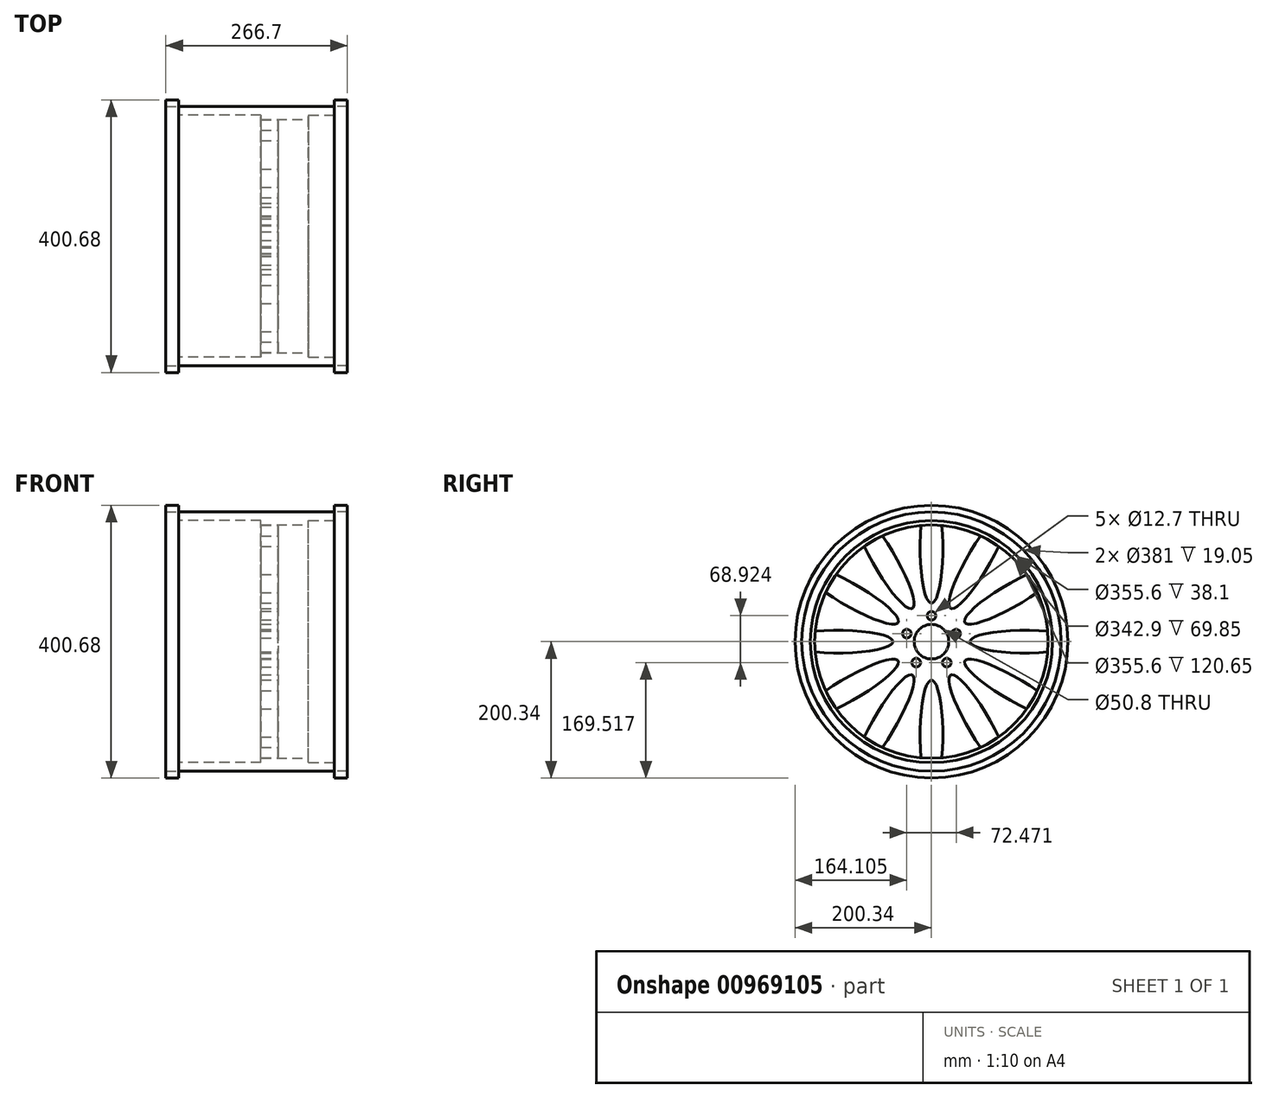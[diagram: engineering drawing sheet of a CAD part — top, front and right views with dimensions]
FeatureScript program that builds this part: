
annotation { "Feature Type Name" : "Feature", "Feature Type Description" : "" }
export const myFeature = defineFeature(function(context is Context, id is Id, definition is map)
    precondition{}
    {
        {
            var Q0;
            Q0=qCreatedBy(makeId("Right.planeOp"),FACE);
            var sketch = newSketch(context, id + "F0", { "sketchPlane" : qUnion([Q0])});
            skCircle(sketch, "E0", {"center": v(0, 0) * mm, "radius": 190.5 * mm});
            skSolve(sketch);
        }
        {
            var Q0;
            Q0=makeQuery(id+"F0.imprint","IMPRINT",FACE,{"disambiguationData":[TD([[makeQuery(id+"F0.imprint","IMPRINT",EDGE,{"derivedFrom":sQuery(id+"F0.wireOp",EDGE,"E0")}),1.0]])]});
            extrude(context, id + "F1", {"entities" : qUnion([Q0]), "depth" : 228.6 * mm, "offsetDistance" : 25.4 * mm});
        }
        {
            var Q0;
            Q0=makeQuery(id+"F1.opExtrude","CAP_FACE",FACE,{"disambiguationData":[OSD([sQuery(id+"F0.wireOp",EDGE,"E0")])],"isStart":false});
            var sketch = newSketch(context, id + "F2", { "sketchPlane" : qUnion([Q0])});
            skCircle(sketch, "E1", {"center": v(0, 0) * mm, "radius": 200.34 * mm});
            skSolve(sketch);
        }
        {
            var Q0;
            Q0=makeQuery(id+"F2.imprint","IMPRINT",FACE,{"disambiguationData":[TD([[makeQuery(id+"F2.imprint","IMPRINT",EDGE,{"derivedFrom":sQuery(id+"F2.wireOp",EDGE,"E1")}),1.0]])]});
            extrude(context, id + "F3", {"entities" : qUnion([Q0]), "depth" : 19.05 * mm, "offsetDistance" : 25.4 * mm});
        }
        {
            var Q0;
            Q0=makeQuery(id+"F1.opExtrude","CAP_FACE",FACE,{"disambiguationData":[OSD([sQuery(id+"F0.wireOp",EDGE,"E0")])],"isStart":false});
            var sketch = newSketch(context, id + "F4", { "sketchPlane" : qUnion([Q0])});
            skCircle(sketch, "E2", {"center": v(0, 0) * mm, "radius": 177.8 * mm});
            skSolve(sketch);
        }
        {
            var Q0;
            Q0 = qSketchRegion(id + "F4", true);
            extrude(context, id + "F5", {"entities" : qUnion([Q0]), "operationType" : NewBodyOperationType.REMOVE, "oppositeDirection" : true, "depth" : 38.1 * mm, "offsetDistance" : 25.4 * mm});
        }
        {
            var Q0;
            Q0=makeQuery(id+"F5.boolean.opBoolean","COPY",FACE,{"derivedFrom":makeQuery(id+"F5.opExtrude","CAP_FACE",FACE,{"disambiguationData":[OSD([sQuery(id+"F4.wireOp",EDGE,"E2")])],"isStart":false})});
            var sketch = newSketch(context, id + "F6", { "sketchPlane" : qUnion([Q0])});
            skCircle(sketch, "E3", {"center": v(0, 0) * mm, "radius": 171.45 * mm});
            skSolve(sketch);
        }
        {
            var Q0;
            Q0 = qSketchRegion(id + "F6", true);
            extrude(context, id + "F7", {"entities" : qUnion([Q0]), "operationType" : NewBodyOperationType.REMOVE, "oppositeDirection" : true, "depth" : 44.45 * mm, "offsetDistance" : 25.4 * mm});
        }
        {
            var Q0;
            Q0=makeQuery(id+"F1.opExtrude","CAP_FACE",FACE,{"disambiguationData":[OSD([sQuery(id+"F0.wireOp",EDGE,"E0")])],"isStart":true});
            var sketch = newSketch(context, id + "F8", { "sketchPlane" : qUnion([Q0])});
            skCircle(sketch, "E4", {"center": v(0, 0) * mm, "radius": 200.34 * mm});
            skCircle(sketch, "E5", {"center": v(0, 0) * mm, "radius": 190.5 * mm});
            skSolve(sketch);
        }
        {
            var Q0;
            Q0 = qSketchRegion(id + "F8", true);
            extrude(context, id + "F9", {"entities" : qUnion([Q0]), "depth" : 19.05 * mm, "offsetDistance" : 25.4 * mm});
        }
        {
            var Q0;
            Q0=makeQuery(id+"F7.boolean.opBoolean","COPY",FACE,{"derivedFrom":makeQuery(id+"F7.opExtrude","CAP_FACE",FACE,{"disambiguationData":[OSD([sQuery(id+"F6.wireOp",EDGE,"E3")])],"isStart":false})});
            var sketch = newSketch(context, id + "F10", { "sketchPlane" : qUnion([Q0])});
            skSolve(sketch);
        }
        {
            var Q0;
            Q0=qCreatedBy(makeId("Right.planeOp"),FACE);
            var sketch = newSketch(context, id + "F11", { "sketchPlane" : qUnion([Q0])});
            skCircle(sketch, "E6", {"center": v(0, 0) * mm, "radius": 177.8 * mm});
            skSolve(sketch);
        }
        {
            var Q0;
            Q0=makeQuery(id+"F11.imprint","IMPRINT",FACE,{"disambiguationData":[TD([[makeQuery(id+"F11.imprint","IMPRINT",EDGE,{"derivedFrom":sQuery(id+"F11.wireOp",EDGE,"E6")}),1.0]])]});
            extrude(context, id + "F12", {"entities" : qUnion([Q0]), "operationType" : NewBodyOperationType.REMOVE, "depth" : 120.65 * mm, "offsetDistance" : 25.4 * mm});
        }
        {
            var Q0;
            Q0=makeQuery(id+"F10.imprint","IMPRINT",FACE,{"disambiguationData":[TD([[makeQuery(id+"F10.imprint","IMPRINT",EDGE,{"derivedFrom":makeQuery(id+"F7.boolean.opBoolean","COPY",EDGE,{"derivedFrom":makeQuery(id+"F7.opExtrude","CAP_EDGE",EDGE,{"disambiguationData":[OSD([sQuery(id+"F6.wireOp",EDGE,"E3")])],"isStart":false})})}),1.0]])]});
            var sketch = newSketch(context, id + "F13", { "sketchPlane" : qUnion([Q0])});
            skLineSegment(sketch, "E7", {"start": v(193.42, 0) * mm, "end": v(-190.61, 0) * mm, "construction": true});
            skLineSegment(sketch, "E8", {"start": v(0, 239.98) * mm, "end": v(0, -192.55) * mm, "construction": true});
            skCircle(sketch, "E9", {"center": v(0, 0) * mm, "radius": 25.4 * mm});
            skSolve(sketch);
        }
        {
            var Q0;
            Q0 = qSketchRegion(id + "F13", true);
            extrude(context, id + "F14", {"entities" : qUnion([Q0]), "operationType" : NewBodyOperationType.REMOVE, "oppositeDirection" : true, "depth" : 25.4 * mm, "offsetDistance" : 25.4 * mm});
        }
        {
            var Q0;
            Q0=makeQuery(id+"F10.imprint","IMPRINT",FACE,{"disambiguationData":[TD([[makeQuery(id+"F10.imprint","IMPRINT",EDGE,{"derivedFrom":makeQuery(id+"F7.boolean.opBoolean","COPY",EDGE,{"derivedFrom":makeQuery(id+"F7.opExtrude","CAP_EDGE",EDGE,{"disambiguationData":[OSD([sQuery(id+"F6.wireOp",EDGE,"E3")])],"isStart":false})})}),1.0]])]});
            var sketch = newSketch(context, id + "F15", { "sketchPlane" : qUnion([Q0])});
            skCircle(sketch, "E10", {"center": v(0, 38.1) * mm, "radius": 6.35 * mm});
            skCircle(sketch, "E11.1.0", {"center": v(-36.24, 11.77) * mm, "radius": 6.35 * mm});
            skCircle(sketch, "E11.2.0", {"center": v(-22.4, -30.82) * mm, "radius": 6.35 * mm});
            skCircle(sketch, "E11.3.0", {"center": v(22.4, -30.82) * mm, "radius": 6.35 * mm});
            skCircle(sketch, "E11.4.0", {"center": v(36.24, 11.77) * mm, "radius": 6.35 * mm});
            skPoint(sketch, "E11.center", {"position": v(0, 0) * mm});
            skSolve(sketch);
        }
        {
            var Q0;
            Q0 = qSketchRegion(id + "F15", true);
            extrude(context, id + "F16", {"entities" : qUnion([Q0]), "operationType" : NewBodyOperationType.REMOVE, "oppositeDirection" : true, "depth" : 25.4 * mm, "offsetDistance" : 25.4 * mm});
        }
        {
            var Q0;
            Q0=makeQuery(id+"F10.imprint","IMPRINT",FACE,{"disambiguationData":[TD([[makeQuery(id+"F10.imprint","IMPRINT",EDGE,{"derivedFrom":makeQuery(id+"F7.boolean.opBoolean","COPY",EDGE,{"derivedFrom":makeQuery(id+"F7.opExtrude","CAP_EDGE",EDGE,{"disambiguationData":[OSD([sQuery(id+"F6.wireOp",EDGE,"E3")])],"isStart":false})})}),1.0]])]});
            var sketch = newSketch(context, id + "F17", { "sketchPlane" : qUnion([Q0])});
            skArc(sketch, "E12", {"start": v(15.23, 170.77) * mm, "mid": v(0, 171.45) * mm, "end": v(-15.23, 170.77) * mm});
            skEllipticalArc(sketch, "E13", {});
            skEllipticalArc(sketch, "E14.1.0", {});
            skEllipticalArc(sketch, "E14.2.0", {});
            skEllipticalArc(sketch, "E14.3.0", {});
            skEllipticalArc(sketch, "E14.4.0", {});
            skEllipticalArc(sketch, "E14.5.0", {});
            skEllipticalArc(sketch, "E14.6.0", {});
            skEllipticalArc(sketch, "E14.7.0", {});
            skEllipticalArc(sketch, "E14.8.0", {});
            skEllipticalArc(sketch, "E14.9.0", {});
            skEllipticalArc(sketch, "E14.10.0", {});
            skEllipticalArc(sketch, "E14.11.0", {});
            skArc(sketch, "E15.trimOffspring", {"start": v(-72.2, 155.5) * mm, "mid": v(-85.72, 148.48) * mm, "end": v(-98.57, 140.28) * mm});
            skArc(sketch, "E16.trimOffspring", {"start": v(-140.28, 98.57) * mm, "mid": v(-148.48, 85.73) * mm, "end": v(-155.5, 72.2) * mm});
            skArc(sketch, "E17.trimOffspring", {"start": v(98.57, 140.28) * mm, "mid": v(85.73, 148.48) * mm, "end": v(72.2, 155.5) * mm});
            skArc(sketch, "E18.trimOffspring", {"start": v(155.5, 72.2) * mm, "mid": v(148.48, 85.72) * mm, "end": v(140.28, 98.57) * mm});
            skArc(sketch, "E19.trimOffspring", {"start": v(170.77, -15.23) * mm, "mid": v(171.45, 0) * mm, "end": v(170.77, 15.23) * mm});
            skArc(sketch, "E20.trimOffspring", {"start": v(140.28, -98.57) * mm, "mid": v(148.48, -85.73) * mm, "end": v(155.5, -72.2) * mm});
            skArc(sketch, "E21.trimOffspring", {"start": v(72.2, -155.5) * mm, "mid": v(85.72, -148.48) * mm, "end": v(98.57, -140.28) * mm});
            skArc(sketch, "E22.trimOffspring", {"start": v(-15.23, -170.77) * mm, "mid": v(0, -171.45) * mm, "end": v(15.23, -170.77) * mm});
            skArc(sketch, "E23.trimOffspring", {"start": v(-98.57, -140.28) * mm, "mid": v(-85.72, -148.48) * mm, "end": v(-72.2, -155.5) * mm});
            skArc(sketch, "E24.trimOffspring", {"start": v(-155.5, -72.2) * mm, "mid": v(-148.48, -85.72) * mm, "end": v(-140.28, -98.57) * mm});
            skArc(sketch, "E25.trimOffspring", {"start": v(-170.77, 15.23) * mm, "mid": v(-171.45, 0) * mm, "end": v(-170.77, -15.23) * mm});
            const initialGuessF17  = {"E13": [0, 0.13752999901771545, 0, -1, 0.08103451132774353, 0.016695612735164435, 4.2896857811086395, 1.9934995260709454], "E14.1.0": [-0.06876499950885771, 0.11910447293179048, 0.5, -0.8660254037844387, 0.08103451132774353, 0.016695612735164435, 4.2896857811086395, 1.9934995260709454], "E14.2.0": [-0.11910447293179047, 0.06876499950885774, 0.8660254037844386, -0.5, 0.08103451132774353, 0.016695612735164435, 4.2896857811086395, 1.9934995260709454], "E14.3.0": [-0.13752999901771545, 0, 1, 0, 0.08103451132774353, 0.016695612735164435, 4.2896857811086395, 1.9934995260709454], "E14.4.0": [-0.11910447293179048, -0.0687649995088577, 0.8660254037844389, 0.5, 0.08103451132774353, 0.016695612735164435, 4.2896857811086395, 1.9934995260709454], "E14.5.0": [-0.06876499950885771, -0.11910447293179048, 0.5, 0.8660254037844387, 0.08103451132774353, 0.016695612735164435, 4.2896857811086395, 1.9934995260709454], "E14.6.0": [0, -0.13752999901771545, 0, 1, 0.08103451132774353, 0.016695612735164435, 4.2896857811086395, 1.9934995260709454], "E14.7.0": [0.06876499950885769, -0.1191044729317905, -0.5, 0.8660254037844388, 0.08103451132774353, 0.016695612735164435, 4.2896857811086395, 1.9934995260709454], "E14.8.0": [0.11910447293179044, -0.06876499950885778, -0.8660254037844384, 0.5, 0.08103451132774353, 0.016695612735164435, 4.2896857811086395, 1.9934995260709454], "E14.9.0": [0.13752999901771545, 0, -1, 0, 0.08103451132774353, 0.016695612735164435, 4.2896857811086395, 1.9934995260709454], "E14.10.0": [0.11910447293179047, 0.06876499950885774, -0.8660254037844386, -0.5, 0.08103451132774353, 0.016695612735164435, 4.2896857811086395, 1.9934995260709454], "E14.11.0": [0.06876499950885778, 0.11910447293179044, -0.5, -0.8660254037844384, 0.08103451132774353, 0.016695612735164435, 4.2896857811086395, 1.9934995260709454]};
            skSetInitialGuess(sketch, initialGuessF17);
            skSolve(sketch);
        }
        {
            var Q0;
            Q0 = qSketchRegion(id + "F17", true);
            extrude(context, id + "F18", {"entities" : qUnion([Q0]), "operationType" : NewBodyOperationType.REMOVE, "oppositeDirection" : true, "depth" : 25.4 * mm, "offsetDistance" : 25.4 * mm});
        }
    });
